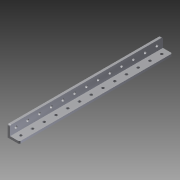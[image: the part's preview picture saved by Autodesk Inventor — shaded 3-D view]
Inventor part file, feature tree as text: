
AUTODESK INVENTOR PART (.ipt)
format: ipt  version: 2013 (Build 170138000, 138)  size: 154,112 bytes
history: native  units: in
note: dims shown in document units (in); Inventor stores cm internally (conversion verified against a paired STEP export)
features: other x1, imported_body x1, extrude x1, fillet x1, sketch x1
ambient origin geometry x8: Origin, YZ Plane, XZ Plane, XY Plane, X Axis, Y Axis, Z Axis, Center Point
feature tree (5):
  other  "ANGLE_288_2011"
  imported_body  "Base1"
  extrude  "Extrusion1"  Depth=0.0787in
  fillet  "Fillet1"  [1 undecoded]
  sketch  "Sketch1"  dims[d0=0.3937in d1=0.0in d2=0.0787in]
note: 1 required parameter value undecoded (feature->parameter linkage not recoverable at this tier; creation-order binding heuristic only, values carry confidence <= 0.55)
